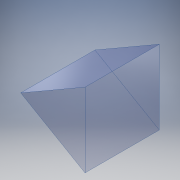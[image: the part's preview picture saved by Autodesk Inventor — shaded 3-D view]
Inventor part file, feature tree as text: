
AUTODESK INVENTOR PART (.ipt)
format: ipt  version: 2017 (Build 210142000, 142)  size: 95,232 bytes
history: native  units: mm
features: extrude x1, sketch x1
ambient origin geometry x8: Origin, YZ Plane, XZ Plane, XY Plane, X Axis, Y Axis, Z Axis, Center Point
bodies: Solid1 (feature_tree)
feature tree (2):
  extrude  "Extrusion1"  Depth=12.7mm TaperAngle=0.0deg
  sketch  "Sketch1"  dims[d0=12.7mm d1=12.7mm d2=0.0mm]
